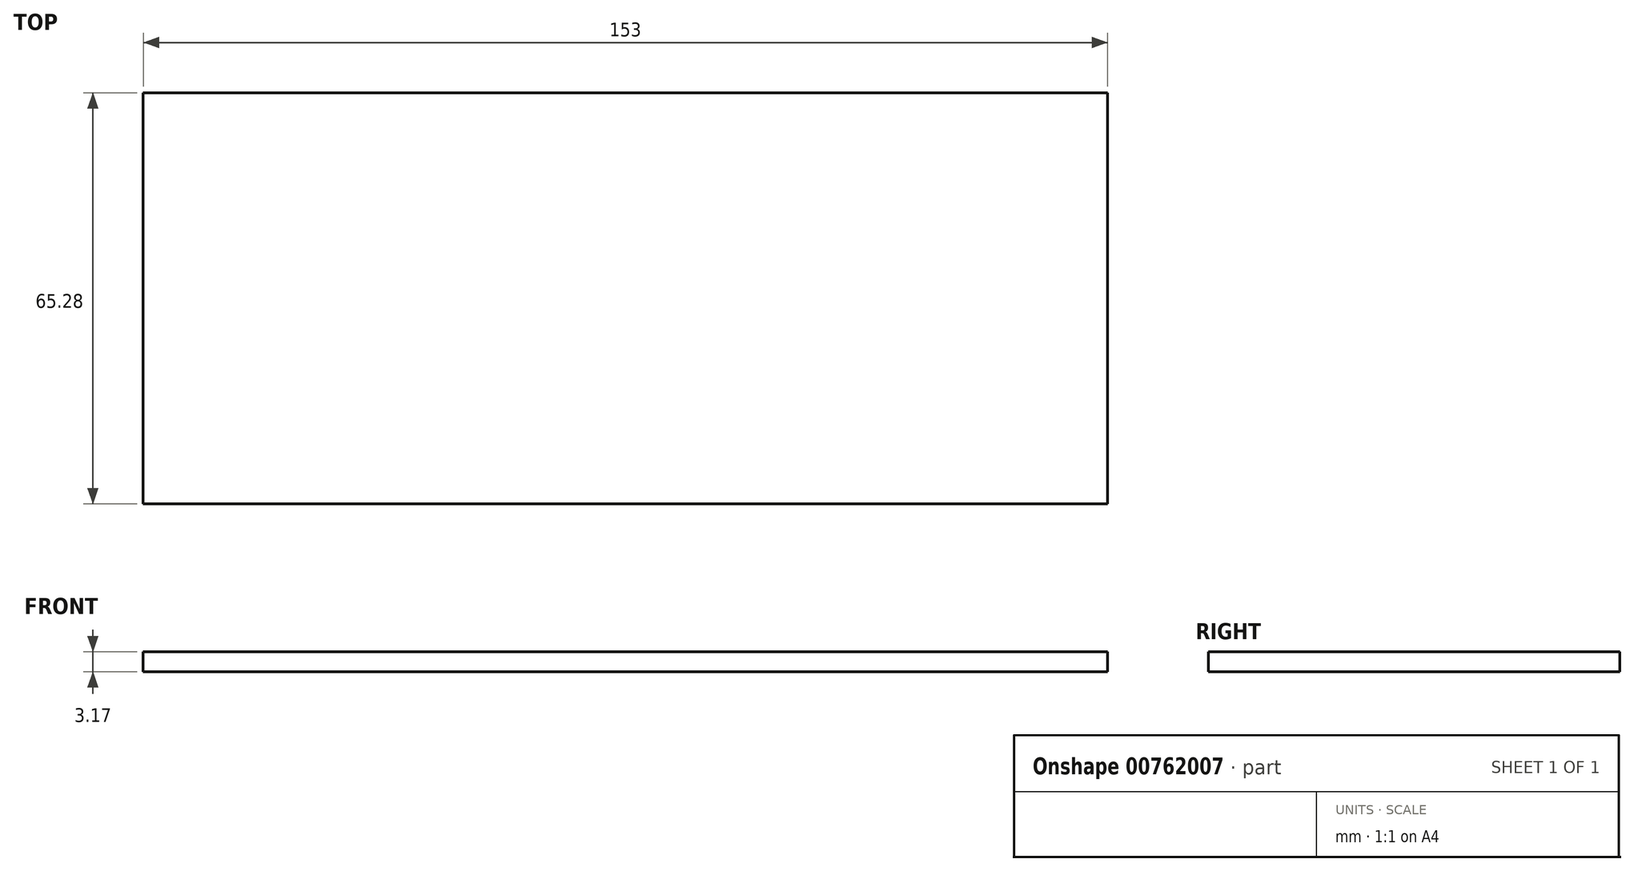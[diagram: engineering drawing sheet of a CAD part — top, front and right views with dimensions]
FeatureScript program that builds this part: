
annotation { "Feature Type Name" : "Feature", "Feature Type Description" : "" }
export const myFeature = defineFeature(function(context is Context, id is Id, definition is map)
    precondition{}
    {
        {
            var Q0;
            Q0=qCreatedBy(makeId("Top.planeOp"),FACE);
            var sketch = newSketch(context, id + "F0", { "sketchPlane" : qUnion([Q0])});
            skLineSegment(sketch, "E0.bottom", {"start": v(-76.5, 32.64) * mm, "end": v(76.5, 32.64) * mm});
            skLineSegment(sketch, "E0.top", {"start": v(-76.5, -32.64) * mm, "end": v(76.5, -32.64) * mm});
            skLineSegment(sketch, "E0.left", {"start": v(-76.5, 32.64) * mm, "end": v(-76.5, -32.64) * mm});
            skLineSegment(sketch, "E0.right", {"start": v(76.5, 32.64) * mm, "end": v(76.5, -32.64) * mm});
            skPoint(sketch, "E0.middle", {"position": v(0, 0) * mm});
            skSolve(sketch);
        }
        {
            var Q0;
            Q0 = qSketchRegion(id + "F0", true);
            extrude(context, id + "F1", {"entities" : qUnion([Q0]), "depth" : 3.17 * mm, "offsetDistance" : 25.4 * mm});
        }
    });
